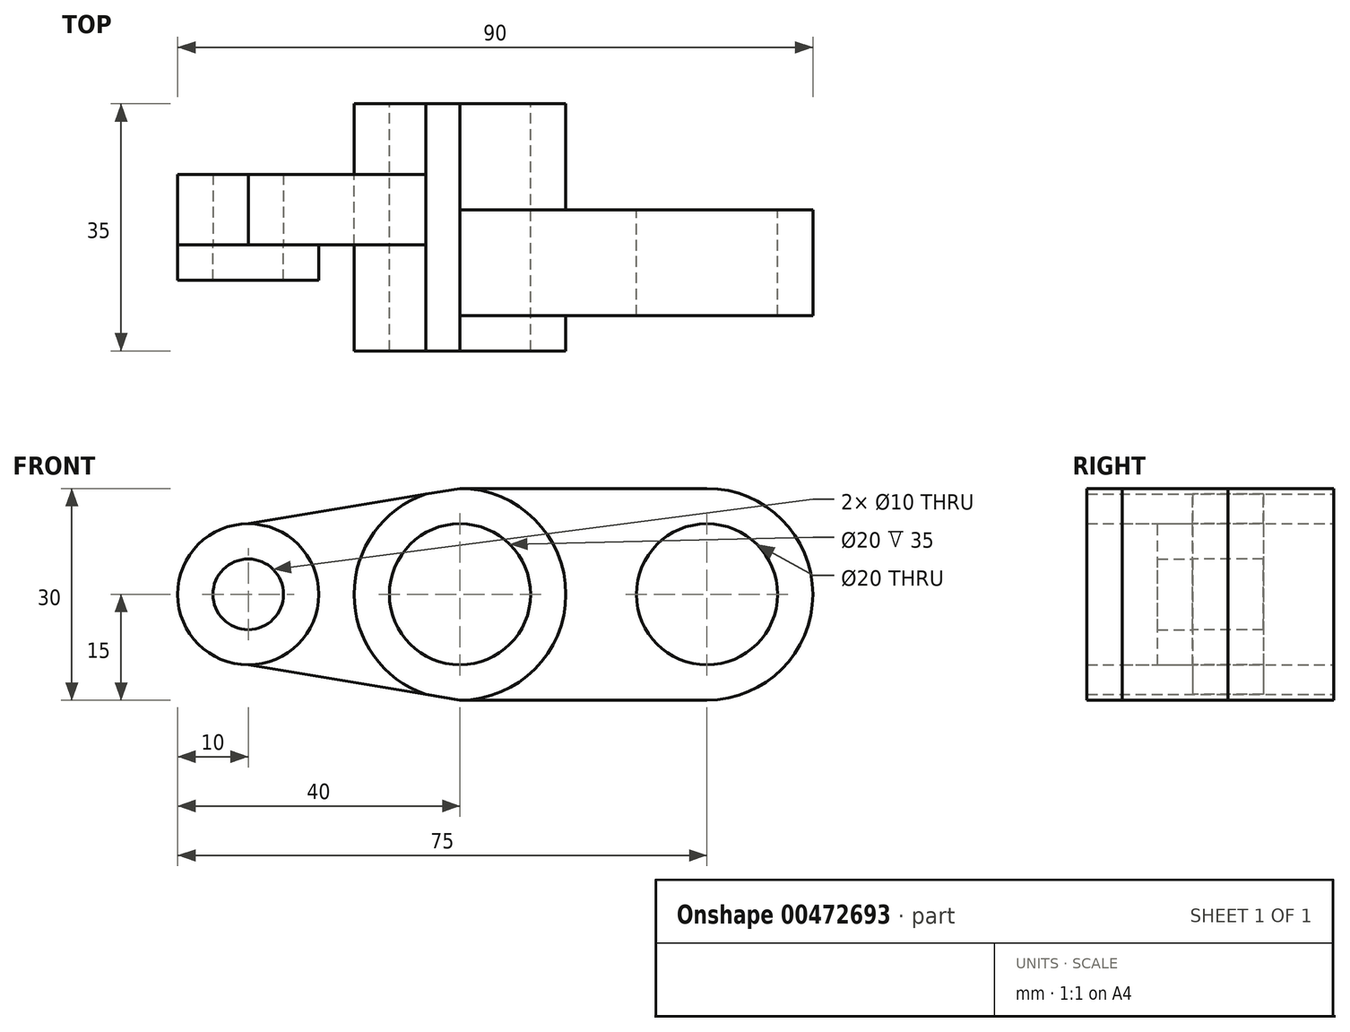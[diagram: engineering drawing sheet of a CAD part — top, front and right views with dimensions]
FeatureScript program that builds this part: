
annotation { "Feature Type Name" : "Feature", "Feature Type Description" : "" }
export const myFeature = defineFeature(function(context is Context, id is Id, definition is map)
    precondition{}
    {
        {
            var Q0;
            Q0=qCreatedBy(makeId("Front.planeOp"),FACE);
            var sketch = newSketch(context, id + "F0", { "sketchPlane" : qUnion([Q0])});
            skCircle(sketch, "E0", {"center": v(0, 0) * mm, "radius": 10 * mm});
            skCircle(sketch, "E1", {"center": v(0, 0) * mm, "radius": 15 * mm});
            skCircle(sketch, "E2", {"center": v(35, 0) * mm, "radius": 10 * mm});
            skCircle(sketch, "E3", {"center": v(35, 0) * mm, "radius": 15 * mm});
            skCircle(sketch, "E4", {"center": v(-30, 0) * mm, "radius": 5 * mm});
            skCircle(sketch, "E5", {"center": v(-30, 0) * mm, "radius": 10 * mm});
            skLineSegment(sketch, "E6", {"start": v(0, 15) * mm, "end": v(35, 15) * mm});
            skLineSegment(sketch, "E7", {"start": v(0, -15) * mm, "end": v(35, -15) * mm});
            skLineSegment(sketch, "E8", {"start": v(-30, 10) * mm, "end": v(0, 15) * mm});
            skLineSegment(sketch, "E9", {"start": v(-30, -10) * mm, "end": v(0, -15) * mm});
            skSolve(sketch);
        }
        {
            var Q0;
            Q0=makeQuery(id+"F0.imprint","IMPRINT",FACE,{"disambiguationData":[TD([[makeQuery(id+"F0.imprint","IMPRINT",EDGE,{"derivedFrom":sQuery(id+"F0.wireOp",EDGE,"E4")}),-1.0]])]});
            extrude(context, id + "F1", {"entities" : qUnion([Q0]), "depth" : 5 * mm});
        }
        {
            var Q0;
            Q0=makeQuery(id+"F0.imprint","IMPRINT",FACE,{"disambiguationData":[TD([[makeQuery(id+"F0.imprint","IMPRINT",EDGE,{"derivedFrom":sQuery(id+"F0.wireOp",EDGE,"E0")}),-1.0]])]});
            extrude(context, id + "F2", {"entities" : qUnion([Q0]), "depth" : 15 * mm});
        }
        {
            var Q0;
            Q0=makeQuery(id+"F0.imprint","IMPRINT",FACE,{"disambiguationData":[TD([[makeQuery(id+"F0.imprint","IMPRINT",EDGE,{"derivedFrom":sQuery(id+"F0.wireOp",EDGE,"E2")}),-1.0]])]});
            var Q1;
            {var subQ0=sQuery(id+"F0.wireOp",EDGE,"E6");Q1=makeQuery(id+"F0.imprint","IMPRINT",FACE,{"disambiguationData":[TD([[makeQuery(id+"F0.imprint","IMPRINT",EDGE,{"derivedFrom":subQ0}),-1.0]])]});}
            extrude(context, id + "F3", {"entities" : qUnion([Q0, Q1]), "operationType" : NewBodyOperationType.ADD, "depth" : 10 * mm});
        }
        {
            var Q0;
            Q0=makeQuery(id+"F0.imprint","IMPRINT",FACE,{"disambiguationData":[TD([[makeQuery(id+"F0.imprint","IMPRINT",EDGE,{"derivedFrom":sQuery(id+"F0.wireOp",EDGE,"E2")}),-1.0]])]});
            var Q1;
            {var subQ0=sQuery(id+"F0.wireOp",EDGE,"E6");Q1=makeQuery(id+"F0.imprint","IMPRINT",FACE,{"disambiguationData":[TD([[makeQuery(id+"F0.imprint","IMPRINT",EDGE,{"derivedFrom":subQ0}),-1.0]])]});}
            extrude(context, id + "F4", {"entities" : qUnion([Q0, Q1]), "operationType" : NewBodyOperationType.ADD, "oppositeDirection" : true, "depth" : 5 * mm});
        }
        {
            var Q0;
            Q0=makeQuery(id+"F0.imprint","IMPRINT",FACE,{"disambiguationData":[TD([[makeQuery(id+"F0.imprint","IMPRINT",EDGE,{"derivedFrom":sQuery(id+"F0.wireOp",EDGE,"E0")}),-1.0]])]});
            extrude(context, id + "F5", {"entities" : qUnion([Q0]), "operationType" : NewBodyOperationType.ADD, "oppositeDirection" : true, "depth" : 20 * mm});
        }
        {
            var Q0;
            Q0=makeQuery(id+"F0.imprint","IMPRINT",FACE,{"disambiguationData":[TD([[makeQuery(id+"F0.imprint","IMPRINT",EDGE,{"derivedFrom":sQuery(id+"F0.wireOp",EDGE,"E4")}),-1.0]])]});
            var Q1;
            {var subQ0=sQuery(id+"F0.wireOp",EDGE,"E8");var subQ1=sQuery(id+"F0.wireOp",EDGE,"E1");var subQ2=makeQuery(id+"F0.imprint","INTERSECT",VERTEX,{"derivedFrom":[subQ1,subQ0]});Q1=makeQuery(id+"F0.imprint","IMPRINT",FACE,{"disambiguationData":[TD([[makeQuery(id+"F0.imprint","IMPRINT",EDGE,{"disambiguationData":[TD([[subQ2,-1.0]])],"derivedFrom":subQ1}),-1.0]])]});}
            extrude(context, id + "F6", {"entities" : qUnion([Q0, Q1]), "oppositeDirection" : true, "depth" : 10 * mm});
        }
    });
